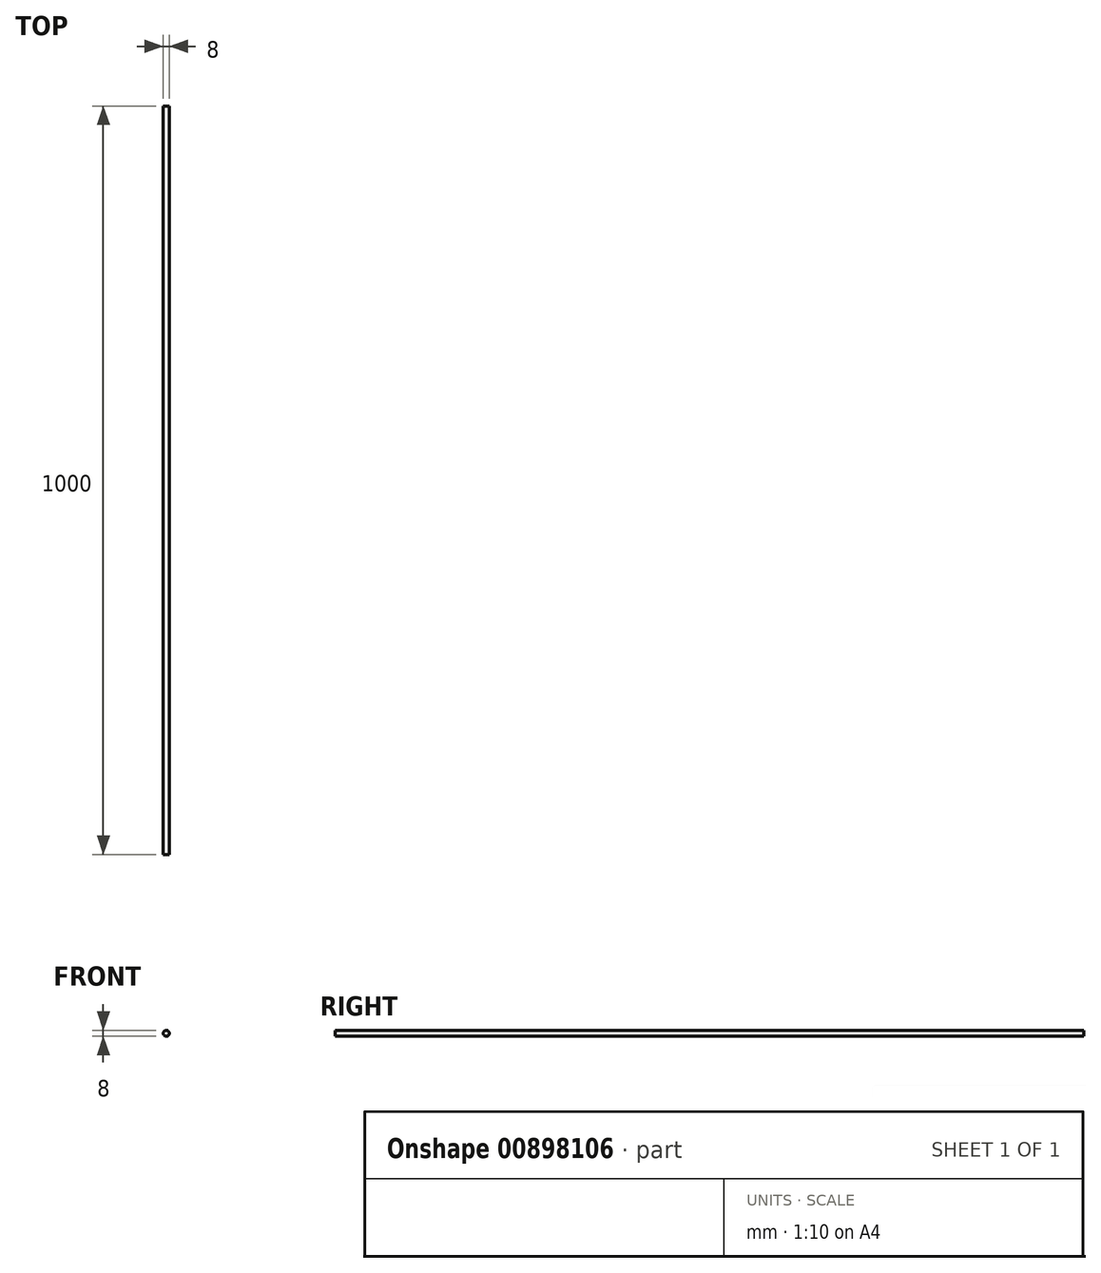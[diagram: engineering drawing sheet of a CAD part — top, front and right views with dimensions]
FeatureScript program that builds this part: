
annotation { "Feature Type Name" : "Feature", "Feature Type Description" : "" }
export const myFeature = defineFeature(function(context is Context, id is Id, definition is map)
    precondition{}
    {
        {
            var Q0;
            Q0=qCreatedBy(makeId("Front.planeOp"),FACE);
            var sketch = newSketch(context, id + "F0", { "sketchPlane" : qUnion([Q0])});
            skCircle(sketch, "E0", {"center": v(0, 0) * mm, "radius": 4 * mm});
            skSolve(sketch);
        }
        {
            var Q0;
            Q0 = qSketchRegion(id + "F0", true);
            extrude(context, id + "F1", {"entities" : qUnion([Q0]), "depth" : 1000 * mm, "offsetDistance" : 25 * mm});
        }
    });
